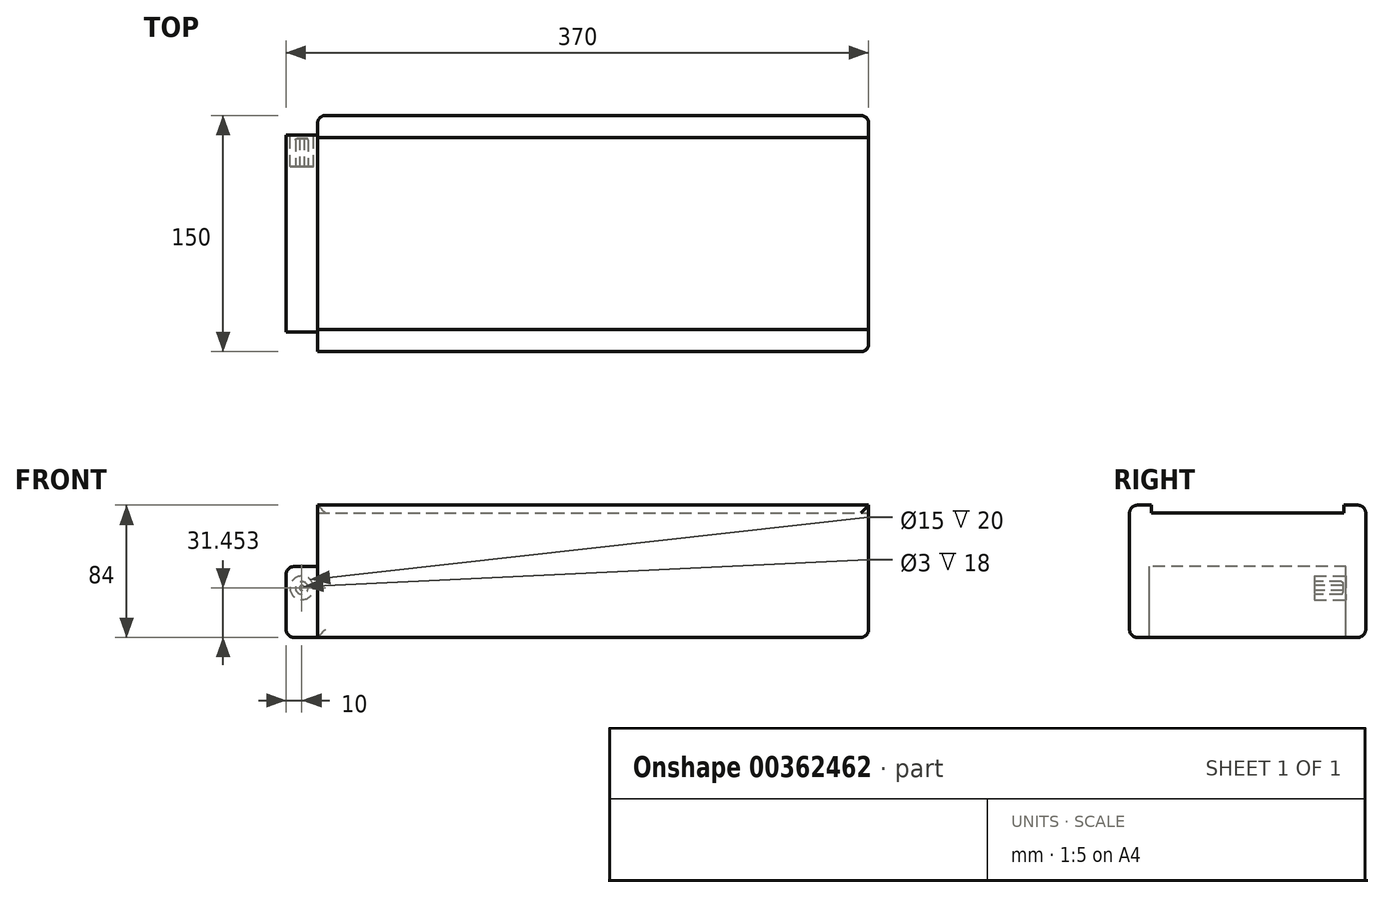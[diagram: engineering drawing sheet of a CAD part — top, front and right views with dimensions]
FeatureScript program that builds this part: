
annotation { "Feature Type Name" : "Feature", "Feature Type Description" : "" }
export const myFeature = defineFeature(function(context is Context, id is Id, definition is map)
    precondition{}
    {
        {
            var Q0;
            Q0=qCreatedBy(makeId("Top.planeOp"),FACE);
            var sketch = newSketch(context, id + "F0", { "sketchPlane" : qUnion([Q0])});
            skLineSegment(sketch, "E0.bottom", {"start": v(0, 0) * mm, "end": v(350, 0) * mm});
            skLineSegment(sketch, "E0.top", {"start": v(0, 150) * mm, "end": v(350, 150) * mm});
            skLineSegment(sketch, "E0.left", {"start": v(0, 0) * mm, "end": v(0, 150) * mm});
            skLineSegment(sketch, "E0.right", {"start": v(350, 0) * mm, "end": v(350, 150) * mm});
            skSolve(sketch);
        }
        {
            var Q0;
            Q0 = qSketchRegion(id + "F0", true);
            extrude(context, id + "F1", {"entities" : qUnion([Q0]), "depth" : 84 * mm});
        }
        {
            var Q0;
            Q0=makeQuery(id+"F1.opExtrude","CAP_FACE",FACE,{"disambiguationData":[OSD([sQuery(id+"F0.wireOp",EDGE,"E0.bottom"),sQuery(id+"F0.wireOp",EDGE,"E0.top"),sQuery(id+"F0.wireOp",EDGE,"E0.left"),sQuery(id+"F0.wireOp",EDGE,"E0.right")])],"isStart":false});
            var sketch = newSketch(context, id + "F2", { "sketchPlane" : qUnion([Q0])});
            skLineSegment(sketch, "E1.bottom", {"start": v(0, 136) * mm, "end": v(350, 136) * mm});
            skLineSegment(sketch, "E1.top", {"start": v(0, 14) * mm, "end": v(350, 14) * mm});
            skLineSegment(sketch, "E1.left", {"start": v(0, 136) * mm, "end": v(0, 14) * mm});
            skLineSegment(sketch, "E1.right", {"start": v(350, 136) * mm, "end": v(350, 14) * mm});
            skSolve(sketch);
        }
        {
            var Q0;
            Q0 = qSketchRegion(id + "F2", true);
            extrude(context, id + "F3", {"entities" : qUnion([Q0]), "operationType" : NewBodyOperationType.REMOVE, "oppositeDirection" : true, "depth" : 5 * mm});
        }
        {
            var Q0;
            Q0=makeQuery(id+"F1.opExtrude","SWEPT_FACE",FACE,{"disambiguationData":[OSD([sQuery(id+"F0.wireOp",EDGE,"E0.left")])]});
            var sketch = newSketch(context, id + "F4", { "sketchPlane" : qUnion([Q0])});
            skLineSegment(sketch, "E2.bottom", {"start": v(-137.5, 0) * mm, "end": v(-12.5, 0) * mm});
            skLineSegment(sketch, "E2.top", {"start": v(-137.5, 45) * mm, "end": v(-12.5, 45) * mm});
            skLineSegment(sketch, "E2.left", {"start": v(-137.5, 0) * mm, "end": v(-137.5, 45) * mm});
            skLineSegment(sketch, "E2.right", {"start": v(-12.5, 0) * mm, "end": v(-12.5, 45) * mm});
            skSolve(sketch);
        }
        {
            var Q0;
            Q0 = qSketchRegion(id + "F4", true);
            extrude(context, id + "F5", {"entities" : qUnion([Q0]), "operationType" : NewBodyOperationType.ADD, "depth" : 20 * mm});
        }
        {
            var Q0;
            Q0=makeQuery(id+"F5.opExtrude","SWEPT_FACE",FACE,{"disambiguationData":[OSD([sQuery(id+"F4.wireOp",EDGE,"E2.left")])]});
            var sketch = newSketch(context, id + "F6", { "sketchPlane" : qUnion([Q0])});
            skLineSegment(sketch, "E3", {"start": v(10, 45) * mm, "end": v(10, 0) * mm, "construction": true});
            skCircle(sketch, "E4", {"center": v(10, 31.45) * mm, "radius": 7.5 * mm});
            skSolve(sketch);
        }
        {
            var Q0;
            Q0 = qSketchRegion(id + "F6", true);
            extrude(context, id + "F7", {"entities" : qUnion([Q0]), "operationType" : NewBodyOperationType.REMOVE, "oppositeDirection" : true, "depth" : 20 * mm});
        }
        {
            var Q0;
            Q0=makeQuery(id+"F7.boolean.opBoolean","COPY",FACE,{"derivedFrom":makeQuery(id+"F7.opExtrude","CAP_FACE",FACE,{"disambiguationData":[OSD([sQuery(id+"F6.wireOp",EDGE,"E4")])],"isStart":false})});
            var sketch = newSketch(context, id + "F8", { "sketchPlane" : qUnion([Q0])});
            skCircle(sketch, "E5", {"center": v(10, 31.45) * mm, "radius": 4 * mm});
            skCircle(sketch, "E6", {"center": v(10, 31.45) * mm, "radius": 1.5 * mm});
            skSolve(sketch);
        }
        {
            var Q0;
            Q0 = qSketchRegion(id + "F8", true);
            extrude(context, id + "F9", {"entities" : qUnion([Q0]), "operationType" : NewBodyOperationType.ADD, "depth" : 18 * mm});
        }
        {
            var Q0;
            Q0=makeQuery(id+"F1.opExtrude","CAP_EDGE",EDGE,{"disambiguationData":[OSD([sQuery(id+"F0.wireOp",EDGE,"E0.top")])],"isStart":false});
            var Q1;
            Q1=makeQuery(id+"F1.opExtrude","CAP_EDGE",EDGE,{"disambiguationData":[OSD([sQuery(id+"F0.wireOp",EDGE,"E0.top")])],"isStart":true});
            var Q2;
            Q2=makeQuery(id+"F1.opExtrude","CAP_EDGE",EDGE,{"disambiguationData":[OSD([sQuery(id+"F0.wireOp",EDGE,"E0.bottom")])],"isStart":false});
            var Q3;
            Q3=makeQuery(id+"F1.opExtrude","CAP_EDGE",EDGE,{"disambiguationData":[OSD([sQuery(id+"F0.wireOp",EDGE,"E0.bottom")])],"isStart":true});
            var Q4;
            Q4=makeQuery(id+"F1.opExtrude","SWEPT_EDGE",EDGE,{"disambiguationData":[OSD([sQuery(id+"F0.wireOp",EDGE,"E0.top"),sQuery(id+"F0.wireOp",EDGE,"E0.right")])]});
            var Q5;
            Q5=makeQuery(id+"F1.opExtrude","CAP_EDGE",EDGE,{"disambiguationData":[OSD([sQuery(id+"F0.wireOp",EDGE,"E0.right")])],"isStart":true});
            var Q6;
            Q6=makeQuery(id+"F3.boolean.opBoolean","COPY",EDGE,{"derivedFrom":makeQuery(id+"F3.opExtrude","CAP_EDGE",EDGE,{"disambiguationData":[OSD([sQuery(id+"F2.wireOp",EDGE,"E1.right")])],"isStart":false})});
            var Q7;
            Q7=makeQuery(id+"F1.opExtrude","SWEPT_EDGE",EDGE,{"disambiguationData":[OSD([sQuery(id+"F0.wireOp",EDGE,"E0.bottom"),sQuery(id+"F0.wireOp",EDGE,"E0.right")])]});
            var Q8;
            Q8=makeQuery(id+"F3.boolean.opBoolean","COPY",EDGE,{"derivedFrom":makeQuery(id+"F3.opExtrude","CAP_EDGE",EDGE,{"disambiguationData":[OSD([sQuery(id+"F2.wireOp",EDGE,"E1.left")])],"isStart":false})});
            var Q9;
            Q9=makeQuery(id+"F1.opExtrude","SWEPT_EDGE",EDGE,{"disambiguationData":[OSD([sQuery(id+"F0.wireOp",EDGE,"E0.top"),sQuery(id+"F0.wireOp",EDGE,"E0.left")])]});
            var Q10;
            Q10=makeQuery(id+"F5.opExtrude","CAP_EDGE",EDGE,{"disambiguationData":[OSD([sQuery(id+"F4.wireOp",EDGE,"E2.top")])],"isStart":false});
            var Q11;
            Q11=makeQuery(id+"F5.opExtrude","CAP_EDGE",EDGE,{"disambiguationData":[OSD([sQuery(id+"F4.wireOp",EDGE,"E2.bottom")])],"isStart":false});
            fillet(context, id + "F10", {"entities" : qUnion([Q0, Q1, Q2, Q3, Q4, Q5, Q6, Q7, Q8, Q9, Q10, Q11]), "radius" : 5 * mm, "tangentPropagation" : true, "allowEdgeOverflow" : false});
        }
        {
            var Q0;
            Q0=makeQuery(id+"F9.opExtrude","CAP_EDGE",EDGE,{"disambiguationData":[OSD([sQuery(id+"F8.wireOp",EDGE,"E5")])],"isStart":false});
            fillet(context, id + "F11", {"entities" : qUnion([Q0]), "radius" : 1 * mm, "tangentPropagation" : true, "allowEdgeOverflow" : false});
        }
    });
